# Revit family: PGR_Noken_WtrSplyFitngsForWshBsnsAndTrghs_NKConcept-FM
name_source: partatom
category: Aparatos sanitarios
revit_build: Autodesk Revit 2017 (Build: 20171027_0315(x64)
units: mm (PartAtom-declared; Revit-internal decimal feet)

## family parameters
Compartido = No
Corte con vacíos al cargar = No
Cota de conector redondo = Diámetro de uso
Número OmniClass = 23.45.55.17
Punto de cálculo de habitación = No
Se basa en plano de trabajo = Sí
Siempre vertical = Sí
Tipo de pieza = Normal
Título OmniClass = Mixing Faucets

## types (1)
- NK-Concept-100149208+100149141
    AccessibilityPerformance = See ProductInformation for technical PDF
    ApplicationType = Basin
    AssetType = Fixed
    BIMObjectName = PGR_Noken_WaterSupplyFittingsForWashBasinsAndTroughs_NKConcept_Chrome-50x320x1084 mm-100149208
    BodyMaterial = Brass
    CWFU = 0
    Category = Pr_40_20_87_98: Washbasin taps
    CloseOffRating = 0.0 Pa
    CodePerformance = EN 817, EN 248
    Collection = NK Concept
    Color = Chrome
    Descripción = Nk Concept. Floor mounted single lever basin mixer. Ø40 mm ceramic cartridge. Flow rate 5 L/min at 3 bar. It has to be purchased together with floormounted Smart box 100149141-N199999397. Without pop-up waste. Material brass, finish chrome plated, nominal lenght 145 mm, nominal width 92 mm, nominal height 1084 mm, net product weight 11 kg. 5 years warranty for superficial finishes and 2 years for the rest of components. EN 817, EN 248
    DiameterCW = 20 mm
    DiameterHW = 20 mm
    DurationUnit = year
    Elevación por defecto = 0 mm  [stored 0 ft]
    FaucetFunction = Mixed
    FaucetOperation = LeverHandle
    FaucetTopDescription = Lever
    FaucetType = Unset
    Features = See ProductInformation for technical PDF
    Finish = Chrome
    FlowCoefficient = 5
    FlowPressure = 0.0
    HWFU = 0
    IfcExportAs = IfcValveType
    IfcExportType = Faucet
    Imagen de tipo = <Ninguno>
    InletConnectionDiameter = 1/2"
    ManufacturerURL = www.noken.com
    Material = Brass
    MaterialMetal = PGR_Noken_Brass_Chrome
    ModelNumber = 100149208
    ModelReference = MONM. NK CONCEPT I/PAV. LAV. CROMO
    Modelo = 100149208
    NBSDescription = Water supply fittings for wash basins and troughs
    NBSReference = 45-35-70/371
    Name = WaterSupplyFittingsForWashBasinsAndTroughs_NKConcept_Chrome-50x320x1084 mm-100149208
    NettWeight = 11
    NominalHeight = 1084 mm  [stored 3.55643 ft]
    NominalLength = 320 mm  [stored 1.04987 ft]
    NominalWidth = 50 mm
    NumberOfConnections = 2
    ProductInformation = http://calidad.info-grupo.com:8081
    Reference = -
    Size = 50x320x1084 mm
    Status = Unset
    SustainabilityPerformance = See ProductInformation for technical PDF
    TechnicalDrawing = See ProductInformation for technical PDF
    TestPressure = 0.0 Pa
    URL = www.noken.com
    Uniclass2015Code = Pr_40_20_87_98
    Uniclass2015Title = Washbasin taps
    Uniclass2015Version = V1_9
    ValveMechanism = Unset
    ValveOperation = Single lever mixer
    ValvePattern = Unset
    Version = 1
    WarrantyDescription = See ProductInformation for technical PDF
    WarrantyDurationUnit = year

note: source unit labels omitted for FlowPressure — the stored unit's dimension contradicts the parameter name (converter mislabeling)

note: [stored X ft] marks values corroborated as IEEE doubles in the binary element streams (Revit-internal decimal feet)

## geometry (parser evidence)
native form markers: Blend x2, Sweep x3
no freeform markers — native parametric forms only
